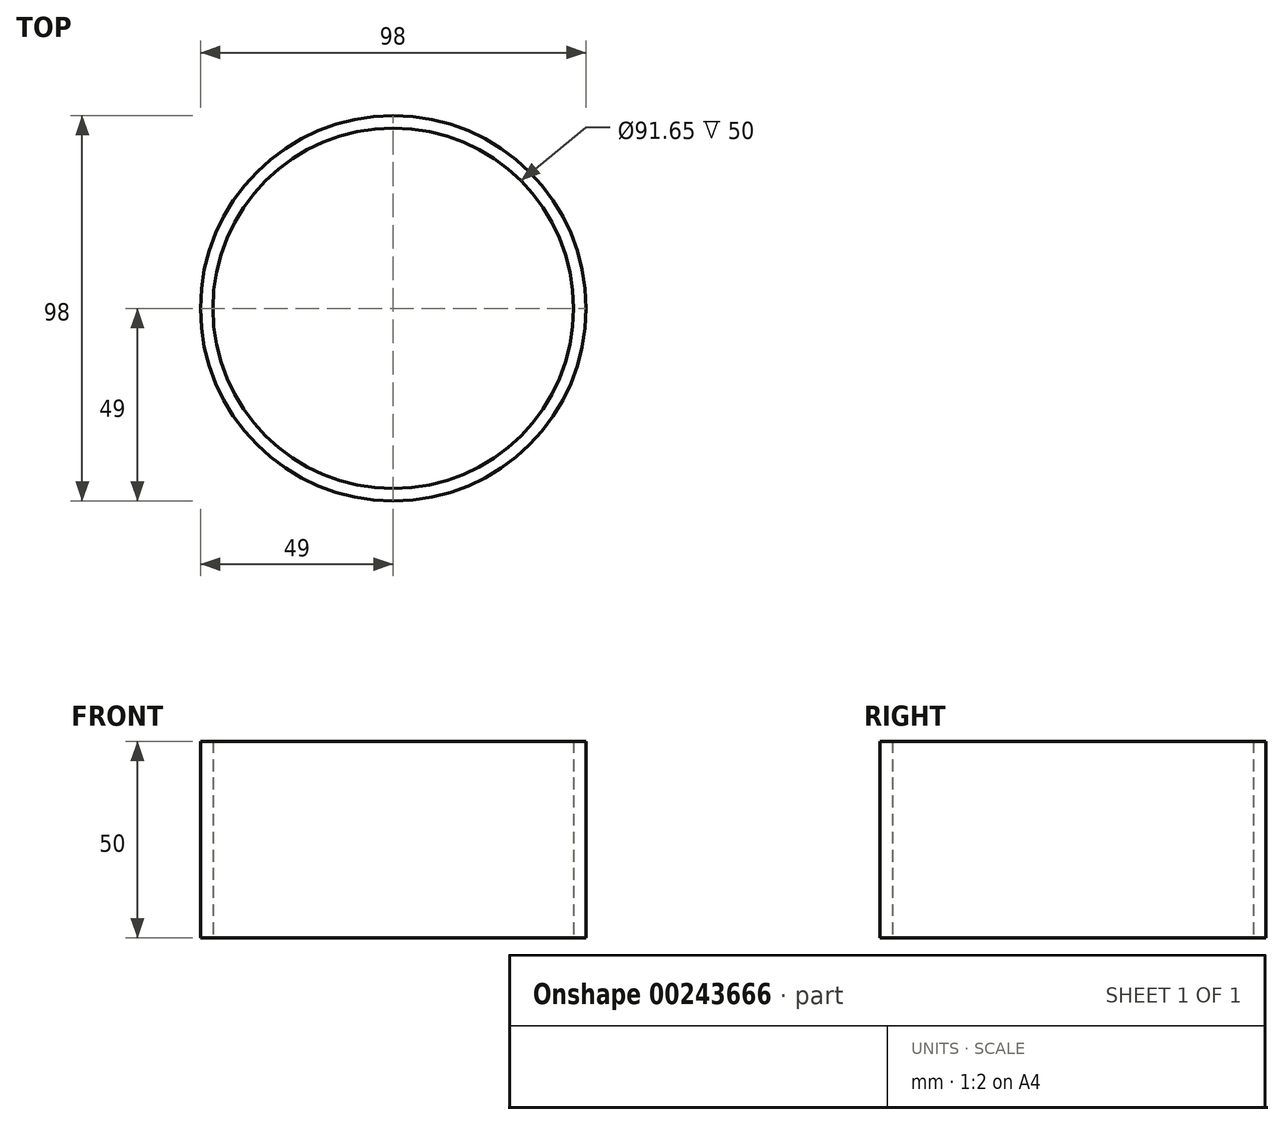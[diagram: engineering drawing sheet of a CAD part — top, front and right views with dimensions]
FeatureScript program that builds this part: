
annotation { "Feature Type Name" : "Feature", "Feature Type Description" : "" }
export const myFeature = defineFeature(function(context is Context, id is Id, definition is map)
    precondition{}
    {
        {
            var Q0;
            Q0=qCreatedBy(makeId("Top.planeOp"),FACE);
            var sketch = newSketch(context, id + "F0", { "sketchPlane" : qUnion([Q0])});
            skCircle(sketch, "E0", {"center": v(0, 0) * mm, "radius": 49 * mm});
            skCircle(sketch, "E1", {"center": v(0, 0) * mm, "radius": 45.83 * mm});
            skSolve(sketch);
        }
        {
            var Q0;
            Q0=qSketchRegion(id+"F0",true);
            extrude(context, id + "F1", {"entities" : qUnion([Q0]), "endBound" : BoundingType.SYMMETRIC, "depth" : 50 * mm});
        }
    });
